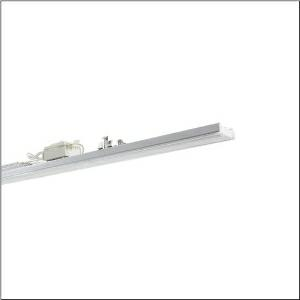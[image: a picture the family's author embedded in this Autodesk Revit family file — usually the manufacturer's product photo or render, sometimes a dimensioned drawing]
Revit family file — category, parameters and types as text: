
# Revit family: licross_r__11_recessed_mo_51te18dv4e5g_e61a
name_source: partatom
category: Lighting Fixtures
units: mm (PartAtom-declared; Revit-internal decimal feet)

## family parameters
Cut with Voids When Loaded = No
Host = Face
Light Source = No
Part Type = Normal
Room Calculation Point = No
Round Connector Dimension = Use Diameter
Shared = No

## types (1)
- --- (1 x LED, 14920 lm, 84.1 W, 4000K)
    Apparent Load = 84 VA
    CIE Flux Codes = 83 96 99 100 100
    Color Rendering = 80
    Color Temperature = 4000K
    Default Elevation = 1800 mm
    Description = Licross® 11 Recessed MO, luminaire insert, of sheet steel, galvanised, coil coated, white, length: 2.250mm, width: 66mm, height: 67mm, LED rated luminous flux: 14.920lm, light colour: 840, control gear: DALI 2, with plug, 5-pole, with phase selection, mains connection: 220..240V, AC, 50/60Hz, rated input power: 84W, internal wiring halogen-free, primary light control with lens, of plastic, primary optical cover: cover, of PMMA, light emission: direct distribution, primary light characteristic: symmetric, protection rating (complete): IP54, insulation class (complete): insulation class I (protective earthing), certification: CE, ENEC, VDE, UKCA, protection symbol: D if used in an environment with non-conductive dust loads with corresponding accessories, impact resistance: IK06, permissible ambient temperature for indoor applications: -25..+35°C, corresponds to IFS (International Featured Standards) requirements for safety and quality in the food industry, reducing of maximum allowable ambient temperature of 5°C with ceiling mounting, LABS conformity tested according to VDMA 24364:2018-05, packaging unit: 1 piece
    Height = 58 mm
    Lamp = 1 x LED
    Lamp Light Flux = 14920 lm
    Lamp Power = 84.1 W
    Lamp count = 1
    Length = 2250 mm
    Luminous efficacy = 177 lm/W
    Manufacturer = Siteco
    ModVariant = No
    Model = 51TE18DV4E5G
    Mounting Place = Ceiling
    Mounting Type = Pendant
    Number of Poles = 1
    OnlyDefault = Yes
    Power Factor = 1
    Product Name = Licross® 11 Recessed MO
    Product group = luminaire insert | ceiling pendant
    ProductGroupID = 902
    Protection Class = Protection class I
    Protection Degree = IP 54
    RLX_Detail_Level = 1
    RLX_Emergency_Light_Flux = 0 lm
    RLX_Emergency_Type = 0
    RLX_Emergency_Type_DB = No
    RlxData = <blob elided: 29321 chars, md5=dd105aae>
    Socket = socket
    Standby Power = 0 W
    System Light Flux = 14920 lm
    System Power = 84 W
    Type Comments = factory setting: luminous flux: 100 % | dim-lin: 254 | 378 mA
    Type Image = l_1296930.jpg
    URL = http://relux.com
    VarID = @adj_120419
    Voltage = 0 V
    Weight = 0.00 kg
    Width = 66 mm

## geometry (parser evidence)
native form markers: Blend x4, Sweep x9
no freeform markers — native parametric forms only
